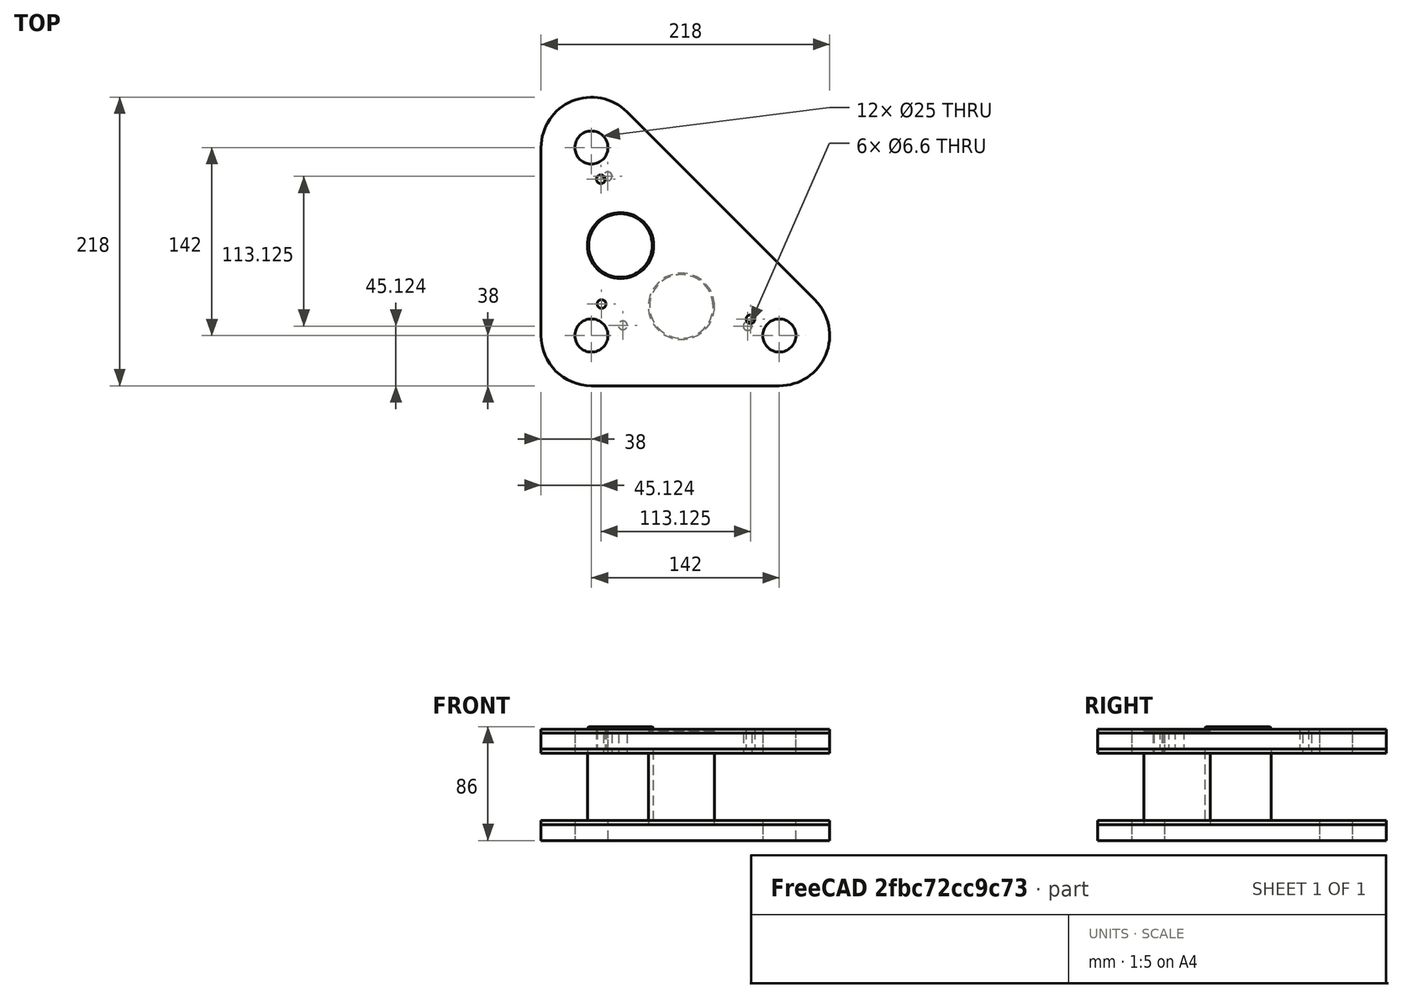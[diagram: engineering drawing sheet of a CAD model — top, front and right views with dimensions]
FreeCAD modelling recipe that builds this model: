
FCSTD DOCUMENT  (FreeCAD 0.21R33668 +26 (Git))
Label: hovairGuidageTriangle
License: All rights reserved
LicenseURL: http://en.wikipedia.org/wiki/All_rights_reserved
objects: TechDraw::DrawViewDimension×35, TechDraw::DrawViewAnnotation×11, Sketcher::SketchObject×9, PartDesign::Pad×6, TechDraw::DrawProjGroupItem×5, TechDraw::DrawSVGTemplate×3, TechDraw::DrawProjGroup×3, TechDraw::DrawViewSection×3, TechDraw::DrawPage×3, PartDesign::Plane×2, PartDesign::Hole×2, PartDesign::Chamfer×2, PartDesign::Body×2, TechDraw::DrawViewBalloon×1
note: 91 computed .brp shape members not serialized (recipe doc carries the construction recipe); baked Part::Feature solids carry a one-line shape summary decoded from their .brp

FEATURE [Sketcher::SketchObject] Sketch006
  FullyConstrained = true
  MapMode = 5
  Support = -> [XY_Plane003]
  sketch-geometry (10):
    g0: ArcOfCircle CenterX=38 CenterY=38 CenterZ=0 NormalX=0 NormalY=0 NormalZ=1 AngleXU=0 Radius=38 StartAngle=3.14159 EndAngle=4.71239
    g1: ArcOfCircle CenterX=180 CenterY=38 CenterZ=0 NormalX=0 NormalY=0 NormalZ=1 AngleXU=0 Radius=38 StartAngle=4.71239 EndAngle=7.06858
    g2: LineSegment StartX=38 StartY=0 StartZ=0 EndX=180 EndY=0 EndZ=0
    g3: ArcOfCircle CenterX=38 CenterY=180 CenterZ=0 NormalX=0 NormalY=0 NormalZ=1 AngleXU=0 Radius=38 StartAngle=0.785398 EndAngle=3.14159
    g4: LineSegment StartX=64.8701 StartY=206.87 StartZ=0 EndX=206.87 EndY=64.8701 EndZ=0
    g5: LineSegment StartX=0 StartY=180 StartZ=0 EndX=0 EndY=38 EndZ=0
    g6: Circle CenterX=38 CenterY=180 CenterZ=0 NormalX=0 NormalY=0 NormalZ=1 AngleXU=0 Radius=12.5
    g7: Circle CenterX=180 CenterY=38 CenterZ=0 NormalX=0 NormalY=0 NormalZ=1 AngleXU=0 Radius=12.5
    g8: Circle CenterX=38 CenterY=38 CenterZ=0 NormalX=0 NormalY=0 NormalZ=1 AngleXU=0 Radius=12.5
    g9: Circle CenterX=106 CenterY=60 CenterZ=0 NormalX=0 NormalY=0 NormalZ=1 AngleXU=0 Radius=25
  constraints (26):
    c: Radius(g0) = 38
    c: Tangent(g0,g-2) = 1.5708
    c: Tangent(g0,g-1) = -1.5708
    c: Radius(g1) = 38
    c: Tangent(g1,g-1) = -1.5708
    c: Distance(g0,g1) = 142
    c: Coincident(g2,g1)
    c: Coincident(g2,g0)
    c: Radius(g3) = 38
    c: Tangent(g3,g-2) = 1.5708
    c: Tangent(g1,g4) = 1.5708
    c: Tangent(g3,g4) = 1.5708
    c: Coincident(g5,g0)
    c: Coincident(g5,g3)
    c: Coincident(g4,g3)
    c: Coincident(g4,g1)
    c: Distance(g0,g3) = 142
    c: Coincident(g3,g6)
    c: Diameter(g6) = 25
    c: Coincident(g7,g1)
    c: Diameter(g7) = 25
    c: Coincident(g8,g0)
    c: Diameter(g8) = 25
    c: Diameter(g9) = 50
    c: DistanceY(g0,g9) = 60
    c: DistanceX(g0,g9) = 106
FEATURE [PartDesign::Pad] Pad001  label="base de fixation des axes"
  Direction = (0,0,1)
  Length = 12
  Length2 = 10
  Profile = -> Sketch006
  ReferenceAxis = -> Sketch006 [N_Axis]
  Type = 0
FEATURE [Sketcher::SketchObject] Sketch
  ExternalGeometry = -> [Sketch006]
  FullyConstrained = true
  MapMode = 5
  Placement = pos=(0,0,0) rot=(1,0,0;3.14159rad)
  Support = -> [Pad001]
  sketch-geometry (1):
    g0: Circle CenterX=106 CenterY=-60 CenterZ=0 NormalX=0 NormalY=0 NormalZ=1 AngleXU=0 Radius=25
  constraints (2):
    c: Coincident(g0,g-3)
    c: Equal(g0,g-3)
FEATURE [PartDesign::Pad] Pad  label="Entretoise"
  BaseFeature = -> Pad001
  Direction = (0,0,-1)
  Length = 83
  Length2 = 10
  Profile = -> Sketch
  ReferenceAxis = -> Sketch [N_Axis]
  Reversed = true
  Type = 0
FEATURE [PartDesign::Plane] DatumPlane  label="planBase"
  AttachmentOffset = pos=(0,0,54) rot=(0,0,1;0rad)
  Length = 60
  MapMode = 5
  Placement = pos=(0,0,66) rot=(0,0,1;0rad)
  ResizeMode = 0
  Support = -> [Pad]
  Width = 60
FEATURE [Sketcher::SketchObject] Sketch007
  FullyConstrained = true
  MapMode = 5
  Placement = pos=(0,0,66) rot=(0,0,1;0rad)
  Support = -> [DatumPlane]
  expr: Constraints[0] = Sketch006.Constraints[0]
  expr: Constraints[16] = Sketch006.Constraints[16]
  expr: Constraints[18] = Sketch006.Constraints[18]
  expr: Constraints[20] = Sketch006.Constraints[20]
  expr: Constraints[22] = Sketch006.Constraints[22]
  expr: Constraints[23] = Sketch006.Constraints[23]
  expr: Constraints[24] = Sketch006.Constraints[24]
  expr: Constraints[25] = Sketch006.Constraints[25]
  expr: Constraints[3] = Sketch006.Constraints[3]
  expr: Constraints[5] = Sketch006.Constraints[5]
  expr: Constraints[8] = Sketch006.Constraints[8]
  sketch-geometry (10):
    g0: ArcOfCircle CenterX=38 CenterY=38 CenterZ=0 NormalX=0 NormalY=0 NormalZ=1 AngleXU=0 Radius=38 StartAngle=3.14159 EndAngle=4.71239
    g1: ArcOfCircle CenterX=180 CenterY=38 CenterZ=0 NormalX=0 NormalY=0 NormalZ=1 AngleXU=0 Radius=38 StartAngle=4.71239 EndAngle=7.06858
    g2: LineSegment StartX=38 StartY=0 StartZ=0 EndX=180 EndY=0 EndZ=0
    g3: ArcOfCircle CenterX=38 CenterY=180 CenterZ=0 NormalX=0 NormalY=0 NormalZ=1 AngleXU=0 Radius=38 StartAngle=0.785398 EndAngle=3.14159
    g4: LineSegment StartX=64.8701 StartY=206.87 StartZ=0 EndX=206.87 EndY=64.8701 EndZ=0
    g5: LineSegment StartX=0 StartY=180 StartZ=0 EndX=0 EndY=38 EndZ=0
    g6: Circle CenterX=38 CenterY=180 CenterZ=0 NormalX=0 NormalY=0 NormalZ=1 AngleXU=0 Radius=12.5
    g7: Circle CenterX=180 CenterY=38 CenterZ=0 NormalX=0 NormalY=0 NormalZ=1 AngleXU=0 Radius=12.5
    g8: Circle CenterX=38 CenterY=38 CenterZ=0 NormalX=0 NormalY=0 NormalZ=1 AngleXU=0 Radius=12.5
    g9: Circle CenterX=106 CenterY=60 CenterZ=0 NormalX=0 NormalY=0 NormalZ=1 AngleXU=0 Radius=25
  constraints (26):
    c: Radius(g0) = 38
    c: Tangent(g0,g-2) = 1.5708
    c: Tangent(g0,g-1) = -1.5708
    c: Radius(g1) = 38
    c: Tangent(g1,g-1) = -1.5708
    c: Distance(g0,g1) = 142
    c: Coincident(g2,g1)
    c: Coincident(g2,g0)
    c: Radius(g3) = 38
    c: Tangent(g3,g-2) = 1.5708
    c: Tangent(g1,g4) = 1.5708
    c: Tangent(g3,g4) = 1.5708
    c: Coincident(g5,g0)
    c: Coincident(g5,g3)
    c: Coincident(g4,g3)
    c: Coincident(g4,g1)
    c: Distance(g0,g3) = 142
    c: Coincident(g3,g6)
    c: Diameter(g6) = 25
    c: Coincident(g7,g1)
    c: Diameter(g7) = 25
    c: Coincident(g8,g0)
    c: Diameter(g8) = 25
    c: Diameter(g9) = 50
    c: DistanceY(g0,g9) = 60
    c: DistanceX(g0,g9) = 106
FEATURE [PartDesign::Pad] Pad002
  BaseFeature = -> Pad
  Direction = (0,0,1)
  Length = 15
  Length2 = 10
  Profile = -> Sketch007
  ReferenceAxis = -> Sketch007 [N_Axis]
  Type = 0
FEATURE [Sketcher::SketchObject] Sketch008
  ExternalGeometry = -> [Pad002]
  FullyConstrained = false
  MapMode = 5
  Placement = pos=(0,0,81) rot=(0,0,1;0rad)
  Support = -> [Pad002]
  sketch-geometry (9):
    g0: LineSegment StartX=-92.9805 StartY=411.142 StartZ=0 EndX=245.063 EndY=-185.406 EndZ=0
    g1: LineSegment StartX=243.321 StartY=104.427 StartZ=0 EndX=-106.422 EndY=-8.72462 EndZ=0
    g2: LineSegment StartX=-89.2896 StartY=118.059 StartZ=0 EndX=316.645 EndY=-2.62407 EndZ=0
    g3: GeomPoint X=50.3253 Y=158.249 Z=0
    g4: GeomPoint X=61.7861 Y=45.6955 Z=0
    g5: GeomPoint X=156.037 Y=45.1243 Z=0
    g6: Circle CenterX=50.3253 CenterY=158.249 CenterZ=0 NormalX=0 NormalY=0 NormalZ=1 AngleXU=0 Radius=2.5
    g7: Circle CenterX=156.037 CenterY=45.1243 CenterZ=0 NormalX=0 NormalY=0 NormalZ=1 AngleXU=0 Radius=2.5
    g8: Circle CenterX=61.7861 CenterY=45.6955 CenterZ=0 NormalX=0 NormalY=0 NormalZ=1 AngleXU=0 Radius=2.5
  constraints (18):
    c: PointOnObject(g-3,g0)
    c: PointOnObject(g-6,g0)
    c: PointOnObject(g-6,g1)
    c: PointOnObject(g-4,g1)
    c: PointOnObject(g-5,g2)
    c: PointOnObject(g-6,g2)
    c: PointOnObject(g5,g2)
    c: PointOnObject(g3,g0)
    c: PointOnObject(g4,g1)
    c: Distance(g4,g-4) = 25
    c: Distance(g5,g-5) = 25
    c: Distance(g3,g-3) = 25
    c: Coincident(g6,g3)
    c: Coincident(g7,g5)
    c: Coincident(g8,g4)
    c: Diameter(g8) = 5
    c: Equal(g8,g6)
    c: Equal(g8,g7)
FEATURE [PartDesign::Hole] Hole
  BaseFeature = -> Pad002
  CustomThreadClearance = 0
  Depth = 15
  DepthType = 0
  Diameter = 6.6
  DrillForDepth = false
  DrillPoint = 1
  DrillPointAngle = 118
  HoleCutCountersinkAngle = 90
  HoleCutCustomValues = false
  HoleCutDepth = 0
  HoleCutDiameter = 0
  HoleCutType = 0
  ModelThread = false
  Profile = -> Sketch008
  Tapered = false
  TaperedAngle = 90
  ThreadClass = 0
  ThreadDepth = 15
  ThreadDepthType = 0
  ThreadDirection = 0
  ThreadFit = 0
  ThreadSize = 14
  ThreadType = 1
  Threaded = false
  UseCustomThreadClearance = false
FEATURE [PartDesign::Chamfer] Chamfer
  Angle = 45
  Base = -> Hole [Edge70]
  BaseFeature = -> Hole
  ChamferType = 0
  FlipDirection = false
  Size = 1
  Size2 = 1
  SupportTransform = false
  UseAllEdges = false
FEATURE [Sketcher::SketchObject] Sketch010
  FullyConstrained = true
  MapMode = 5
  Support = -> [XY_Plane004]
  sketch-geometry (10):
    g0: ArcOfCircle CenterX=38 CenterY=38 CenterZ=0 NormalX=0 NormalY=0 NormalZ=1 AngleXU=0 Radius=38 StartAngle=3.14159 EndAngle=4.71239
    g1: ArcOfCircle CenterX=180 CenterY=38 CenterZ=0 NormalX=0 NormalY=0 NormalZ=1 AngleXU=0 Radius=38 StartAngle=4.71239 EndAngle=7.06858
    g2: LineSegment StartX=38 StartY=0 StartZ=0 EndX=180 EndY=0 EndZ=0
    g3: ArcOfCircle CenterX=38 CenterY=180 CenterZ=0 NormalX=0 NormalY=0 NormalZ=1 AngleXU=0 Radius=38 StartAngle=0.785398 EndAngle=3.14159
    g4: LineSegment StartX=64.8701 StartY=206.87 StartZ=0 EndX=206.87 EndY=64.8701 EndZ=0
    g5: LineSegment StartX=0 StartY=180 StartZ=0 EndX=0 EndY=38 EndZ=0
    g6: Circle CenterX=38 CenterY=180 CenterZ=0 NormalX=0 NormalY=0 NormalZ=1 AngleXU=0 Radius=12.5
    g7: Circle CenterX=180 CenterY=38 CenterZ=0 NormalX=0 NormalY=0 NormalZ=1 AngleXU=0 Radius=12.5
    g8: Circle CenterX=38 CenterY=38 CenterZ=0 NormalX=0 NormalY=0 NormalZ=1 AngleXU=0 Radius=12.5
    g9: Circle CenterX=60 CenterY=106 CenterZ=0 NormalX=0 NormalY=0 NormalZ=1 AngleXU=0 Radius=25
  constraints (26):
    c: Radius(g0) = 38
    c: Tangent(g0,g-2) = 1.5708
    c: Tangent(g0,g-1) = -1.5708
    c: Radius(g1) = 38
    c: Tangent(g1,g-1) = -1.5708
    c: Distance(g0,g1) = 142
    c: Coincident(g2,g1)
    c: Coincident(g2,g0)
    c: Radius(g3) = 38
    c: Tangent(g3,g-2) = 1.5708
    c: Tangent(g1,g4) = 1.5708
    c: Tangent(g3,g4) = 1.5708
    c: Coincident(g5,g0)
    c: Coincident(g5,g3)
    c: Coincident(g4,g3)
    c: Coincident(g4,g1)
    c: Distance(g0,g3) = 142
    c: Coincident(g3,g6)
    c: Diameter(g6) = 25
    c: Coincident(g7,g1)
    c: Diameter(g7) = 25
    c: Coincident(g8,g0)
    c: Diameter(g8) = 25
    c: Diameter(g9) = 50
    c: DistanceY(g0,g9) = 106
    c: DistanceX(g0,g9) = 60
FEATURE [PartDesign::Pad] Pad004  label="base de fixation des axes001"
  Direction = (0,0,1)
  Length = 15
  Length2 = 10
  Profile = -> Sketch010
  ReferenceAxis = -> Sketch010 [N_Axis]
  Type = 0
FEATURE [Sketcher::SketchObject] Sketch009
  ExternalGeometry = -> [Sketch010]
  FullyConstrained = true
  MapMode = 5
  Placement = pos=(0,0,0) rot=(1,0,0;3.14159rad)
  Support = -> [Pad004]
  sketch-geometry (1):
    g0: Circle CenterX=60 CenterY=-106 CenterZ=0 NormalX=0 NormalY=0 NormalZ=1 AngleXU=0 Radius=25
  constraints (2):
    c: Coincident(g0,g-3)
    c: Equal(g0,g-3)
FEATURE [PartDesign::Pad] Pad003  label="Entretoise001"
  BaseFeature = -> Pad004
  Direction = (0,0,-1)
  Length = 86
  Length2 = 10
  Profile = -> Sketch009
  ReferenceAxis = -> Sketch009 [N_Axis]
  Reversed = true
  Type = 0
FEATURE [PartDesign::Plane] DatumPlane001  label="planBase001"
  AttachmentOffset = pos=(0,0,54) rot=(0,0,1;0rad)
  Length = 60
  MapMode = 5
  Placement = pos=(0,0,69) rot=(0,0,1;0rad)
  ResizeMode = 0
  Support = -> [Pad003]
  Width = 60
FEATURE [Sketcher::SketchObject] Sketch011
  FullyConstrained = true
  MapMode = 5
  Placement = pos=(0,0,69) rot=(0,0,1;0rad)
  Support = -> [DatumPlane001]
  expr: Constraints[0] = Sketch010.Constraints[0]
  expr: Constraints[16] = Sketch010.Constraints[16]
  expr: Constraints[18] = Sketch010.Constraints[18]
  expr: Constraints[20] = Sketch010.Constraints[20]
  expr: Constraints[22] = Sketch010.Constraints[22]
  expr: Constraints[23] = Sketch010.Constraints[23]
  expr: Constraints[24] = Sketch010.Constraints[24]
  expr: Constraints[25] = Sketch010.Constraints[25]
  expr: Constraints[3] = Sketch010.Constraints[3]
  expr: Constraints[5] = Sketch010.Constraints[5]
  expr: Constraints[8] = Sketch010.Constraints[8]
  sketch-geometry (10):
    g0: ArcOfCircle CenterX=38 CenterY=38 CenterZ=0 NormalX=0 NormalY=0 NormalZ=1 AngleXU=0 Radius=38 StartAngle=3.14159 EndAngle=4.71239
    g1: ArcOfCircle CenterX=180 CenterY=38 CenterZ=0 NormalX=0 NormalY=0 NormalZ=1 AngleXU=0 Radius=38 StartAngle=4.71239 EndAngle=7.06858
    g2: LineSegment StartX=38 StartY=0 StartZ=0 EndX=180 EndY=0 EndZ=0
    g3: ArcOfCircle CenterX=38 CenterY=180 CenterZ=0 NormalX=0 NormalY=0 NormalZ=1 AngleXU=0 Radius=38 StartAngle=0.785398 EndAngle=3.14159
    g4: LineSegment StartX=64.8701 StartY=206.87 StartZ=0 EndX=206.87 EndY=64.8701 EndZ=0
    g5: LineSegment StartX=0 StartY=180 StartZ=0 EndX=0 EndY=38 EndZ=0
    g6: Circle CenterX=38 CenterY=180 CenterZ=0 NormalX=0 NormalY=0 NormalZ=1 AngleXU=0 Radius=12.5
    g7: Circle CenterX=180 CenterY=38 CenterZ=0 NormalX=0 NormalY=0 NormalZ=1 AngleXU=0 Radius=12.5
    g8: Circle CenterX=38 CenterY=38 CenterZ=0 NormalX=0 NormalY=0 NormalZ=1 AngleXU=0 Radius=12.5
    g9: Circle CenterX=60 CenterY=106 CenterZ=0 NormalX=0 NormalY=0 NormalZ=1 AngleXU=0 Radius=25
  constraints (26):
    c: Radius(g0) = 38
    c: Tangent(g0,g-2) = 1.5708
    c: Tangent(g0,g-1) = -1.5708
    c: Radius(g1) = 38
    c: Tangent(g1,g-1) = -1.5708
    c: Distance(g0,g1) = 142
    c: Coincident(g2,g1)
    c: Coincident(g2,g0)
    c: Radius(g3) = 38
    c: Tangent(g3,g-2) = 1.5708
    c: Tangent(g1,g4) = 1.5708
    c: Tangent(g3,g4) = 1.5708
    c: Coincident(g5,g0)
    c: Coincident(g5,g3)
    c: Coincident(g4,g3)
    c: Coincident(g4,g1)
    c: Distance(g0,g3) = 142
    c: Coincident(g3,g6)
    c: Diameter(g6) = 25
    c: Coincident(g7,g1)
    c: Diameter(g7) = 25
    c: Coincident(g8,g0)
    c: Diameter(g8) = 25
    c: Diameter(g9) = 50
    c: DistanceY(g0,g9) = 106
    c: DistanceX(g0,g9) = 60
FEATURE [PartDesign::Pad] Pad005
  BaseFeature = -> Pad003
  Direction = (0,0,1)
  Length = 15
  Length2 = 10
  Profile = -> Sketch011
  ReferenceAxis = -> Sketch011 [N_Axis]
  Type = 0
FEATURE [Sketcher::SketchObject] Sketch012
  ExternalGeometry = -> [Pad005]
  FullyConstrained = false
  MapMode = 5
  Placement = pos=(0,0,84) rot=(0,0,1;0rad)
  Support = -> [Pad005]
  sketch-geometry (9):
    g0: LineSegment StartX=-29.8325 StartY=408.164 StartZ=0 EndX=147.908 EndY=-189.691 EndZ=0
    g1: LineSegment StartX=139.234 StartY=350.905 StartZ=0 EndX=-31.2765 EndY=-176.127 EndZ=0
    g2: LineSegment StartX=-79.9504 StartY=185.305 StartZ=0 EndX=317.641 EndY=-39.9967 EndZ=0
    g3: GeomPoint X=45.1243 Y=156.037 Z=0
    g4: GeomPoint X=45.6955 Y=61.7861 Z=0
    g5: GeomPoint X=158.249 Y=50.3253 Z=0
    g6: Circle CenterX=45.1243 CenterY=156.037 CenterZ=0 NormalX=0 NormalY=0 NormalZ=1 AngleXU=0 Radius=2.5
    g7: Circle CenterX=158.249 CenterY=50.3253 CenterZ=0 NormalX=0 NormalY=0 NormalZ=1 AngleXU=0 Radius=2.5
    g8: Circle CenterX=45.6955 CenterY=61.7861 CenterZ=0 NormalX=0 NormalY=0 NormalZ=1 AngleXU=0 Radius=2.5
  constraints (18):
    c: PointOnObject(g-3,g0)
    c: PointOnObject(g-6,g0)
    c: PointOnObject(g-6,g1)
    c: PointOnObject(g-4,g1)
    c: PointOnObject(g-5,g2)
    c: PointOnObject(g-6,g2)
    c: PointOnObject(g5,g2)
    c: PointOnObject(g3,g0)
    c: PointOnObject(g4,g1)
    c: Distance(g4,g-4) = 25
    c: Distance(g5,g-5) = 25
    c: Distance(g3,g-3) = 25
    c: Coincident(g6,g3)
    c: Coincident(g7,g5)
    c: Coincident(g8,g4)
    c: Diameter(g8) = 5
    c: Equal(g8,g6)
    c: Equal(g8,g7)
FEATURE [PartDesign::Hole] Hole001
  BaseFeature = -> Pad005
  CustomThreadClearance = 0
  Depth = 15
  DepthType = 0
  Diameter = 6.6
  DrillForDepth = false
  DrillPoint = 1
  DrillPointAngle = 118
  HoleCutCountersinkAngle = 90
  HoleCutCustomValues = false
  HoleCutDepth = 0
  HoleCutDiameter = 6.1
  HoleCutType = 0
  ModelThread = false
  Profile = -> Sketch012
  Tapered = false
  TaperedAngle = 90
  ThreadClass = 0
  ThreadDepth = 15
  ThreadDepthType = 0
  ThreadDirection = 0
  ThreadFit = 0
  ThreadSize = 14
  ThreadType = 1
  Threaded = false
  UseCustomThreadClearance = false
FEATURE [PartDesign::Chamfer] Chamfer001
  Angle = 45
  Base = -> Hole001 [Edge70]
  BaseFeature = -> Hole001
  ChamferType = 0
  FlipDirection = false
  Size = 1
  Size2 = 1
  SupportTransform = false
  UseAllEdges = false
FEATURE [PartDesign::Body] Body003  label="triangleGauche"
  Group = -> [Sketch010,Pad004,Sketch009,Pad003,DatumPlane001,Sketch011,Pad005,Sketch012,Hole001,Chamfer001]
  Origin = -> Origin004
  Tip = -> Chamfer001
FEATURE [TechDraw::DrawSVGTemplate] Template
  EditableTexts = Designed_by_Name=Designed by Name; Drawing_number=Drawing number; FC-Date=Date; FC-SC=Scale; FC-SH=Sheet; FC-Title=Title; Subtitle=Subtitle; Weight=Weight
  Height = 210
  Orientation = 1
  Width = 297
  expr: Label = Template
FEATURE [TechDraw::DrawProjGroupItem] ProjItem  label="Front"
  CoarseView = false
  Direction = (0,0,1)
  Focus = 100
  HardHidden = false
  IsoCount = 0
  IsoHidden = false
  IsoVisible = true
  LockPosition = true
  Perspective = false
  Rotation = 0
  RotationVector = (-1,0,0)
  Scale = 0.5
  ScaleType = 2
  ScrubCount = 0
  SeamHidden = false
  SeamVisible = true
  SmoothHidden = false
  SmoothVisible = true
  Source = -> [Chamfer]
  Type = 0
  X = 0
  XDirection = (2e-16,-1,0)
  Y = 0
FEATURE [TechDraw::DrawProjGroupItem] ProjItem001  label="Left"
  CoarseView = false
  Direction = (-2e-16,1,1e-16)
  Focus = 100
  HardHidden = false
  IsoCount = 0
  IsoHidden = false
  IsoVisible = true
  LockPosition = false
  Perspective = false
  Rotation = 0
  RotationVector = (1,0,0)
  ScaleType = 2
  ScrubCount = 0
  SeamHidden = false
  SeamVisible = true
  SmoothHidden = false
  SmoothVisible = true
  Source = -> [Chamfer]
  Type = 1
  X = 90.25
  XDirection = (0,-1e-16,1)
  Y = 0
FEATURE [TechDraw::DrawProjGroup] ProjGroup
  Anchor = -> ProjItem
  AutoDistribute = true
  LockPosition = false
  ProjectionType = 0
  Rotation = 0
  Scale = 0.5
  ScaleType = 0
  Source = -> [Chamfer]
  Views = -> [ProjItem,ProjItem001]
  X = 94.985
  Y = 133.767
  spacingX = 15
  spacingY = 15
FEATURE [TechDraw::DrawViewDimension] Dimension
  AngleOverride = false
  Arbitrary = false
  ArbitraryTolerances = false
  EqualTolerance = true
  ExtensionAngle = 0
  FormatSpec = %.2w
  FormatSpecOverTolerance = %+.2w
  FormatSpecUnderTolerance = %+.2w
  Inverted = false
  LineAngle = 0
  LockPosition = false
  MeasureType = 1
  OverTolerance = 0
  References2D = -> [ProjItem001]
  Rotation = 0
  Scale = 0.5
  ScaleType = 0
  TheoreticalExact = false
  Type = 1
  UnderTolerance = 0
  X = -2.20172
  Y = -62.1546
FEATURE [TechDraw::DrawViewDimension] Dimension003
  AngleOverride = false
  Arbitrary = false
  ArbitraryTolerances = false
  EqualTolerance = true
  ExtensionAngle = 0
  FormatSpec = %.2w
  FormatSpecOverTolerance = %+.2w
  FormatSpecUnderTolerance = %+.2w
  Inverted = false
  LineAngle = 0
  LockPosition = false
  MeasureType = 1
  OverTolerance = 0
  References2D = -> [ProjItem001]
  Rotation = 0
  Scale = 0.5
  ScaleType = 0
  TheoreticalExact = false
  Type = 1
  UnderTolerance = 0
  X = 51.2517
  Y = 24.673
FEATURE [Sketcher::SketchObject] Sketch013
  ExternalGeometry = -> [Chamfer]
  FullyConstrained = false
  MapMode = 5
  Placement = pos=(0,0,81) rot=(0,0,1;0rad)
  Support = -> [Chamfer]
  sketch-geometry (5):
    g0: LineSegment StartX=0 StartY=158.249 StartZ=0 EndX=50.3253 EndY=158.249 EndZ=0
    g1: LineSegment StartX=50.3253 StartY=158.249 StartZ=0 EndX=50.3253 EndY=45.6955 EndZ=0
    g2: LineSegment StartX=50.3253 StartY=45.6955 StartZ=0 EndX=144.123 EndY=45.6955 EndZ=0
    g3: LineSegment StartX=144.123 StartY=45.1243 StartZ=0 EndX=236.221 EndY=45.1243 EndZ=0
    g4: LineSegment StartX=144.123 StartY=45.6955 StartZ=0 EndX=144.123 EndY=45.1243 EndZ=0
  constraints (13):
    c: Coincident(g0,g-3)
    c: Horizontal(g0)
    c: PointOnObject(g0,g-2)
    c: Coincident(g1,g0)
    c: Vertical(g1)
    c: Coincident(g2,g1)
    c: PointOnObject(g-4,g2)
    c: Horizontal(g2)
    c: Horizontal(g3)
    c: PointOnObject(g-5,g3)
    c: Coincident(g4,g3)
    c: Coincident(g2,g4)
    c: Vertical(g4)
FEATURE [PartDesign::Body] Body002  label="triangle droit"
  Group = -> [Sketch006,Pad001,Sketch,Pad,DatumPlane,Sketch007,Pad002,Sketch008,Hole,Chamfer,Sketch013]
  Origin = -> Origin003
  Tip = -> Chamfer
FEATURE [TechDraw::DrawViewDimension] Dimension004
  AngleOverride = false
  Arbitrary = false
  ArbitraryTolerances = false
  EqualTolerance = true
  ExtensionAngle = 0
  FormatSpec = R%.2w
  FormatSpecOverTolerance = %+.2w
  FormatSpecUnderTolerance = %+.2w
  Inverted = false
  LineAngle = 0
  LockPosition = false
  MeasureType = 1
  OverTolerance = 0
  References2D = -> [ProjItem]
  Rotation = 0
  Scale = 0.5
  ScaleType = 0
  TheoreticalExact = false
  Type = 4
  UnderTolerance = 0
  X = 54.0861
  Y = 56.9792
FEATURE [TechDraw::DrawViewDimension] Dimension005
  AngleOverride = false
  Arbitrary = true
  ArbitraryTolerances = false
  EqualTolerance = true
  ExtensionAngle = 0
  FormatSpec = M6
  FormatSpecOverTolerance = %+.2w
  FormatSpecUnderTolerance = %+.2w
  Inverted = false
  LineAngle = 0
  LockPosition = false
  MeasureType = 1
  OverTolerance = 0
  References2D = -> [ProjItem]
  Rotation = 0
  Scale = 0.5
  ScaleType = 0
  TheoreticalExact = false
  Type = 5
  UnderTolerance = 0
  X = 13.1733
  Y = 30.3827
FEATURE [TechDraw::DrawViewDimension] Dimension006
  AngleOverride = false
  Arbitrary = false
  ArbitraryTolerances = false
  EqualTolerance = true
  ExtensionAngle = 0
  FormatSpec = ⌀%.2w
  FormatSpecOverTolerance = %+.2w
  FormatSpecUnderTolerance = %+.2w
  Inverted = false
  LineAngle = 0
  LockPosition = false
  MeasureType = 1
  OverTolerance = 0
  References2D = -> [ProjItem]
  Rotation = 0
  Scale = 0.5
  ScaleType = 0
  TheoreticalExact = false
  Type = 5
  UnderTolerance = 0
  X = 18.3828
  Y = 42.1273
FEATURE [TechDraw::DrawViewDimension] Dimension007
  AngleOverride = false
  Arbitrary = true
  ArbitraryTolerances = false
  EqualTolerance = true
  ExtensionAngle = 0
  FormatSpec = 200
  Inverted = false
  LineAngle = 0
  LockPosition = false
  MeasureType = 1
  OverTolerance = 0
  References2D = -> [ProjItem]
  Rotation = 0
  Scale = 0.5
  ScaleType = 0
  TheoreticalExact = false
  Type = 0
  UnderTolerance = 0
  X = -18.8935
  Y = 32.6274
FEATURE [TechDraw::DrawViewDimension] Dimension008
  AngleOverride = false
  Arbitrary = false
  ArbitraryTolerances = false
  EqualTolerance = true
  ExtensionAngle = 0
  FormatSpec = %.2w
  FormatSpecOverTolerance = %+.2w
  FormatSpecUnderTolerance = %+.2w
  Inverted = false
  LineAngle = 0
  LockPosition = false
  MeasureType = 1
  OverTolerance = 0
  References2D = -> [ProjItem]
  Rotation = 0
  Scale = 0.5
  ScaleType = 0
  TheoreticalExact = false
  Type = 2
  UnderTolerance = 0
  X = 66.2444
  Y = -39.7903
FEATURE [TechDraw::DrawViewDimension] Dimension009
  AngleOverride = false
  Arbitrary = false
  ArbitraryTolerances = false
  EqualTolerance = true
  ExtensionAngle = 0
  FormatSpec = %.2w
  FormatSpecOverTolerance = %+.2w
  FormatSpecUnderTolerance = %+.2w
  Inverted = false
  LineAngle = 0
  LockPosition = false
  MeasureType = 1
  OverTolerance = 0
  References2D = -> [ProjItem]
  Rotation = 0
  Scale = 0.5
  ScaleType = 0
  TheoreticalExact = false
  Type = 2
  UnderTolerance = 0
  X = 66.4544
  Y = -1.17084
FEATURE [TechDraw::DrawViewDimension] Dimension010
  AngleOverride = false
  Arbitrary = false
  ArbitraryTolerances = false
  EqualTolerance = true
  ExtensionAngle = 0
  FormatSpec = %.2w
  FormatSpecOverTolerance = %+.2w
  FormatSpecUnderTolerance = %+.2w
  Inverted = false
  LineAngle = 0
  LockPosition = false
  MeasureType = 1
  OverTolerance = 0
  References2D = -> [ProjItem]
  Rotation = 0
  Scale = 0.5
  ScaleType = 0
  TheoreticalExact = false
  Type = 1
  UnderTolerance = 0
  X = 45.6795
  Y = -66.2972
FEATURE [TechDraw::DrawViewDimension] Dimension011
  AngleOverride = false
  Arbitrary = false
  ArbitraryTolerances = false
  EqualTolerance = true
  ExtensionAngle = 0
  FormatSpec = %.2w
  FormatSpecOverTolerance = %+.2w
  FormatSpecUnderTolerance = %+.2w
  Inverted = false
  LineAngle = 0
  LockPosition = false
  MeasureType = 1
  OverTolerance = 0
  References2D = -> [ProjItem]
  Rotation = 0
  Scale = 0.5
  ScaleType = 0
  TheoreticalExact = false
  Type = 1
  UnderTolerance = 0
  X = 4.75673
  Y = -64.2585
FEATURE [TechDraw::DrawViewDimension] Dimension012
  AngleOverride = false
  Arbitrary = false
  ArbitraryTolerances = false
  EqualTolerance = true
  ExtensionAngle = 0
  FormatSpec = %.2w
  FormatSpecOverTolerance = %+.2w
  FormatSpecUnderTolerance = %+.2w
  Inverted = false
  LineAngle = 0
  LockPosition = false
  MeasureType = 1
  OverTolerance = 0
  References2D = -> [ProjItem]
  Rotation = 0
  Scale = 0.5
  ScaleType = 0
  TheoreticalExact = false
  Type = 1
  UnderTolerance = 0
  X = 39.9798
  Y = 21.4191
FEATURE [TechDraw::DrawViewDimension] Dimension013
  AngleOverride = false
  Arbitrary = false
  ArbitraryTolerances = false
  EqualTolerance = true
  ExtensionAngle = 0
  FormatSpec = ⌀%.2w
  FormatSpecOverTolerance = %+.2w
  FormatSpecUnderTolerance = %+.2w
  Inverted = false
  LineAngle = 0
  LockPosition = false
  MeasureType = 1
  OverTolerance = 0
  References2D = -> [ProjItem]
  Rotation = 0
  Scale = 0.5
  ScaleType = 0
  TheoreticalExact = false
  Type = 5
  UnderTolerance = 0
  X = -8.25965
  Y = 5.44612
FEATURE [TechDraw::DrawViewDimension] Dimension014
  AngleOverride = false
  Arbitrary = false
  ArbitraryTolerances = false
  EqualTolerance = true
  ExtensionAngle = 0
  FormatSpec = %.2w
  FormatSpecOverTolerance = %+.2w
  FormatSpecUnderTolerance = %+.2w
  Inverted = false
  LineAngle = 0
  LockPosition = false
  MeasureType = 1
  OverTolerance = 0
  References2D = -> [ProjItem]
  Rotation = 0
  Scale = 0.5
  ScaleType = 0
  TheoreticalExact = false
  Type = 2
  UnderTolerance = 0
  X = -4.86799
  Y = -24.4104
FEATURE [TechDraw::DrawViewDimension] Dimension015
  AngleOverride = false
  Arbitrary = false
  ArbitraryTolerances = false
  EqualTolerance = true
  ExtensionAngle = 0
  FormatSpec = %.2w
  FormatSpecOverTolerance = %+.2w
  FormatSpecUnderTolerance = %+.2w
  Inverted = false
  LineAngle = 0
  LockPosition = false
  MeasureType = 1
  OverTolerance = 0
  References2D = -> [ProjItem001]
  Rotation = 0
  Scale = 0.5
  ScaleType = 0
  TheoreticalExact = false
  Type = 1
  UnderTolerance = 0
  X = -1.58253
  Y = -51.3349
FEATURE [TechDraw::DrawViewDimension] Dimension016
  AngleOverride = false
  Arbitrary = false
  ArbitraryTolerances = false
  EqualTolerance = true
  ExtensionAngle = 0
  FormatSpec = %.2w
  FormatSpecOverTolerance = %+.2w
  FormatSpecUnderTolerance = %+.2w
  Inverted = false
  LineAngle = 0
  LockPosition = false
  MeasureType = 1
  OverTolerance = 0
  References2D = -> [ProjItem001]
  Rotation = 0
  Scale = 0.5
  ScaleType = 0
  TheoreticalExact = false
  Type = 1
  UnderTolerance = 0
  X = 28.9686
  Y = 65.6457
FEATURE [TechDraw::DrawViewDimension] Dimension017
  AngleOverride = false
  Arbitrary = false
  ArbitraryTolerances = false
  EqualTolerance = true
  ExtensionAngle = 0
  FormatSpec = %.2w
  FormatSpecOverTolerance = %+.2w
  FormatSpecUnderTolerance = %+.2w
  Inverted = false
  LineAngle = 0
  LockPosition = false
  MeasureType = 1
  OverTolerance = 0
  References2D = -> [ProjItem001]
  Rotation = 0
  Scale = 0.5
  ScaleType = 0
  TheoreticalExact = false
  Type = 1
  UnderTolerance = 0
  X = -31.0511
  Y = 64.9807
FEATURE [TechDraw::DrawViewDimension] Dimension018
  AngleOverride = false
  Arbitrary = false
  ArbitraryTolerances = false
  EqualTolerance = true
  ExtensionAngle = 0
  FormatSpec = %.2w x45°
  FormatSpecOverTolerance = %+.2w
  FormatSpecUnderTolerance = %+.2w
  Inverted = false
  LineAngle = 0
  LockPosition = false
  MeasureType = 1
  OverTolerance = 0
  References2D = -> [ProjItem001]
  Rotation = 0
  Scale = 0.5
  ScaleType = 0
  TheoreticalExact = false
  Type = 2
  UnderTolerance = 0
  X = 30.7283
  Y = -23.2941
FEATURE [TechDraw::DrawViewSection] SectionView  label="Section  - "
  BaseView = -> ProjItem
  CoarseView = false
  CutSurfaceDisplay = 2
  Direction = (1,1e-16,0)
  FileGeomPattern = C:/Program Files/FreeCAD 0.21/data/Mod/TechDraw/PAT/FCPAT.pat
  FileHatchPattern = C:/Program Files/FreeCAD 0.21/data/Mod/TechDraw/Patterns/simple.svg
  Focus = 100
  FuseBeforeCut = false
  HardHidden = false
  HatchOffset = (0,0,0)
  HatchRotation = 0
  HatchScale = 1
  IsoCount = 0
  IsoHidden = false
  IsoVisible = true
  LockPosition = false
  NameGeomPattern = Diamant
  Perspective = false
  Rotation = 0
  Scale = 0.5
  ScaleType = 2
  ScrubCount = 0
  SeamHidden = false
  SeamVisible = true
  SectionDirection = 4
  SectionNormal = (1,1e-16,0)
  SectionOrigin = (38,108,41.5)
  SmoothHidden = false
  SmoothVisible = true
  Source = -> [Chamfer]
  TrimAfterCut = false
  X = 79.928
  XDirection = (1e-16,-1,0)
  Y = 37.3303
FEATURE [TechDraw::DrawPage] Page
  KeepUpdated = true
  NextBalloonIndex = 1
  ProjectionType = 0
  Scale = 0.5
  Template = -> Template
  Views = -> [ProjGroup,Dimension,Dimension003,Dimension004,Dimension005,Dimension006,Dimension007,Dimension008,Dimension009,Dimension010,Dimension011,Dimension012,Dimension013,Dimension014,Dimension015,Dimension016,Dimension017,Dimension018,SectionView]
FEATURE [TechDraw::DrawSVGTemplate] Template001
  EditableTexts = A3=A3; A__=_________; B__=_________; C__=_________; D__=_________; E__=_________; Echelle=0,5; F__=_________; G__=_________; H__=_________; I__=_________; Societe=CAF; Sous_titre=DROIT; Titre=TRIANGLE HOVAIR
  Height = 297
  Orientation = 1
  Template = C:/Program Files/FreeCAD 0.21/data/Mod/TechDraw/Templates/A3_Landscape_FR_m52.svg
  Width = 420
FEATURE [TechDraw::DrawProjGroupItem] ProjItem002  label="Front001"
  CoarseView = false
  Direction = (0,0,1)
  Focus = 100
  HardHidden = false
  IsoCount = 0
  IsoHidden = false
  IsoVisible = true
  LockPosition = true
  Perspective = false
  Rotation = 0
  RotationVector = (1,0,0)
  Scale = 0.5
  ScaleType = 2
  ScrubCount = 0
  SeamHidden = false
  SeamVisible = true
  SmoothHidden = false
  SmoothVisible = true
  Source = -> [Body002]
  Type = 0
  X = 0
  XDirection = (1e-16,-1,0)
  Y = 0
FEATURE [TechDraw::DrawProjGroupItem] ProjItem003  label="Left001"
  CoarseView = false
  Direction = (-1e-16,1,1e-16)
  Focus = 100
  HardHidden = false
  IsoCount = 0
  IsoHidden = false
  IsoVisible = true
  LockPosition = true
  Perspective = false
  Rotation = 0
  RotationVector = (1,0,0)
  Scale = 0.5
  ScaleType = 2
  ScrubCount = 0
  SeamHidden = false
  SeamVisible = true
  SmoothHidden = false
  SmoothVisible = false
  Source = -> [Body002]
  Type = 1
  X = 159.01
  XDirection = (0,-1e-16,1)
  Y = 0
FEATURE [TechDraw::DrawProjGroup] ProjGroup001
  Anchor = -> ProjItem002
  AutoDistribute = true
  LockPosition = true
  ProjectionType = 0
  Rotation = 0
  Scale = 0.5
  ScaleType = 0
  Source = -> [Body002]
  Views = -> [ProjItem002,ProjItem003]
  X = 145.162
  Y = 186.721
  spacingX = 15
  spacingY = 15
FEATURE [TechDraw::DrawViewDimension] Dimension019
  AngleOverride = false
  Arbitrary = false
  ArbitraryTolerances = false
  EqualTolerance = true
  ExtensionAngle = 0
  FormatSpec = R%.2w
  FormatSpecOverTolerance = %+.2w
  FormatSpecUnderTolerance = %+.2w
  Inverted = false
  LineAngle = 0
  LockPosition = false
  MeasureType = 1
  OverTolerance = 0
  References2D = -> [ProjItem002]
  Rotation = 0
  Scale = 0.5
  ScaleType = 0
  TheoreticalExact = false
  Type = 4
  UnderTolerance = 0
  X = 54.9066
  Y = 61.5716
FEATURE [TechDraw::DrawViewDimension] Dimension020
  AngleOverride = false
  Arbitrary = false
  ArbitraryTolerances = false
  EqualTolerance = true
  ExtensionAngle = 0
  FormatSpec = %.2w
  FormatSpecOverTolerance = %+.2w
  FormatSpecUnderTolerance = %+.2w
  Inverted = false
  LineAngle = 0
  LockPosition = false
  MeasureType = 1
  OverTolerance = 0
  References2D = -> [ProjItem002]
  Rotation = 0
  Scale = 0.5
  ScaleType = 0
  TheoreticalExact = false
  Type = 2
  UnderTolerance = 0
  X = 71.9765
  Y = -41.5848
FEATURE [TechDraw::DrawViewDimension] Dimension021
  AngleOverride = false
  Arbitrary = false
  ArbitraryTolerances = false
  EqualTolerance = true
  ExtensionAngle = 0
  FormatSpec = %.2w
  FormatSpecOverTolerance = %+.2w
  FormatSpecUnderTolerance = %+.2w
  Inverted = false
  LineAngle = 0
  LockPosition = false
  MeasureType = 1
  OverTolerance = 0
  References2D = -> [ProjItem002]
  Rotation = 0
  Scale = 0.5
  ScaleType = 0
  TheoreticalExact = false
  Type = 2
  UnderTolerance = 0
  X = 72.0538
  Y = 2.10538
FEATURE [TechDraw::DrawViewDimension] Dimension022
  AngleOverride = false
  Arbitrary = false
  ArbitraryTolerances = false
  EqualTolerance = true
  ExtensionAngle = 0
  FormatSpec = ⌀%.2w
  FormatSpecOverTolerance = %+.2w
  FormatSpecUnderTolerance = %+.2w
  Inverted = false
  LineAngle = 0
  LockPosition = false
  MeasureType = 1
  OverTolerance = 0
  References2D = -> [ProjItem002]
  Rotation = 0
  Scale = 0.5
  ScaleType = 0
  TheoreticalExact = false
  Type = 5
  UnderTolerance = 0
  X = 18.893
  Y = 41.1341
FEATURE [TechDraw::DrawViewDimension] Dimension023
  AngleOverride = false
  Arbitrary = true
  ArbitraryTolerances = false
  EqualTolerance = true
  ExtensionAngle = 0
  FormatSpec = M6
  FormatSpecOverTolerance = %+.2w
  FormatSpecUnderTolerance = %+.2w
  Inverted = false
  LineAngle = 0
  LockPosition = false
  MeasureType = 1
  OverTolerance = 0
  References2D = -> [ProjItem002]
  Rotation = 0
  Scale = 0.5
  ScaleType = 0
  TheoreticalExact = false
  Type = 5
  UnderTolerance = 0
  X = 11.001
  Y = 29.1765
FEATURE [TechDraw::DrawViewDimension] Dimension024
  AngleOverride = false
  Arbitrary = false
  ArbitraryTolerances = false
  EqualTolerance = true
  ExtensionAngle = 0
  FormatSpec = %.2w
  FormatSpecOverTolerance = %+.2w
  FormatSpecUnderTolerance = %+.2w
  Inverted = false
  LineAngle = 0
  LockPosition = false
  MeasureType = 1
  OverTolerance = 0
  References2D = -> [ProjItem002]
  Rotation = 0
  Scale = 0.5
  ScaleType = 0
  TheoreticalExact = false
  Type = 1
  UnderTolerance = 0
  X = 45.6162
  Y = -63.3965
FEATURE [TechDraw::DrawViewDimension] Dimension025
  AngleOverride = false
  Arbitrary = false
  ArbitraryTolerances = false
  EqualTolerance = true
  ExtensionAngle = 0
  FormatSpec = %.2w
  FormatSpecOverTolerance = %+.2w
  FormatSpecUnderTolerance = %+.2w
  Inverted = false
  LineAngle = 0
  LockPosition = false
  MeasureType = 1
  OverTolerance = 0
  References2D = -> [ProjItem002]
  Rotation = 0
  Scale = 0.5
  ScaleType = 0
  TheoreticalExact = false
  Type = 1
  UnderTolerance = 0
  X = 5.08227
  Y = -63.2407
FEATURE [TechDraw::DrawViewDimension] Dimension026
  AngleOverride = false
  Arbitrary = false
  ArbitraryTolerances = false
  EqualTolerance = true
  ExtensionAngle = 0
  FormatSpec = %.2w
  FormatSpecOverTolerance = %+.2w
  FormatSpecUnderTolerance = %+.2w
  Inverted = false
  LineAngle = 0
  LockPosition = false
  MeasureType = 1
  OverTolerance = 0
  References2D = -> [ProjItem002]
  Rotation = 0
  Scale = 0.5
  ScaleType = 0
  TheoreticalExact = false
  Type = 1
  UnderTolerance = 0
  X = 39.166
  Y = 19.237
FEATURE [TechDraw::DrawViewDimension] Dimension027
  AngleOverride = false
  Arbitrary = false
  ArbitraryTolerances = false
  EqualTolerance = true
  ExtensionAngle = 0
  FormatSpec = ⌀%.2w
  FormatSpecOverTolerance = %+.2w
  FormatSpecUnderTolerance = %+.2w
  Inverted = false
  LineAngle = 0
  LockPosition = false
  MeasureType = 1
  OverTolerance = 0
  References2D = -> [ProjItem002]
  Rotation = 0
  Scale = 0.5
  ScaleType = 0
  TheoreticalExact = false
  Type = 5
  UnderTolerance = 0
  X = -8.21447
  Y = 4.0267
FEATURE [TechDraw::DrawViewDimension] Dimension028
  AngleOverride = false
  Arbitrary = false
  ArbitraryTolerances = false
  EqualTolerance = true
  ExtensionAngle = 0
  FormatSpec = %.2w
  FormatSpecOverTolerance = %+.2w
  FormatSpecUnderTolerance = %+.2w
  Inverted = false
  LineAngle = 0
  LockPosition = false
  MeasureType = 1
  OverTolerance = 0
  References2D = -> [ProjItem002]
  Rotation = 0
  Scale = 0.5
  ScaleType = 0
  TheoreticalExact = false
  Type = 2
  UnderTolerance = 0
  X = -0.479657
  Y = -24.8425
FEATURE [TechDraw::DrawViewSection] SectionView001  label="A - A"
  BaseView = -> ProjItem002
  CoarseView = false
  CutSurfaceDisplay = 2
  Direction = (1,0,0)
  FileGeomPattern = C:/Program Files/FreeCAD 0.21/data/Mod/TechDraw/PAT/FCPAT.pat
  FileHatchPattern = C:/Program Files/FreeCAD 0.21/data/Mod/TechDraw/Patterns/simple.svg
  Focus = 100
  FuseBeforeCut = false
  HardHidden = false
  HatchOffset = (0,0,0)
  HatchRotation = 0
  HatchScale = 1
  IsoCount = 0
  IsoHidden = false
  IsoVisible = true
  LockPosition = false
  NameGeomPattern = Diamant
  Perspective = false
  Rotation = 0
  Scale = 0.5
  ScaleType = 2
  ScrubCount = 0
  SeamHidden = false
  SeamVisible = true
  SectionDirection = 4
  SectionNormal = (1,0,0)
  SectionOrigin = (38,109,41.5)
  SmoothHidden = false
  SmoothVisible = true
  Source = -> [Body002]
  TrimAfterCut = false
  X = 146.365
  XDirection = (0,-1,0)
  Y = 48.7904
FEATURE [TechDraw::DrawViewSection] SectionView002  label="B-B"
  BaseView = -> ProjItem002
  CoarseView = false
  CutSurfaceDisplay = 2
  Direction = (1e-16,-1,0)
  FileGeomPattern = C:/Program Files/FreeCAD 0.21/data/Mod/TechDraw/PAT/FCPAT.pat
  FileHatchPattern = C:/Program Files/FreeCAD 0.21/data/Mod/TechDraw/Patterns/simple.svg
  Focus = 100
  FuseBeforeCut = false
  HardHidden = false
  HatchOffset = (0,0,0)
  HatchRotation = 0
  HatchScale = 1
  IsoCount = 0
  IsoHidden = false
  IsoVisible = true
  LockPosition = false
  NameGeomPattern = Diamant
  Perspective = false
  Rotation = 90
  Scale = 0.5
  ScaleType = 2
  ScrubCount = 0
  SeamHidden = false
  SeamVisible = true
  SectionDirection = 4
  SectionNormal = (1e-16,-1,0)
  SectionOrigin = (107,158,41.5)
  SmoothHidden = false
  SmoothVisible = true
  Source = -> [Body002]
  TrimAfterCut = false
  X = 46.1608
  XDirection = (1,1e-16,0)
  Y = 159.91
FEATURE [TechDraw::DrawViewAnnotation] Annotation
  Font = osifont
  LineSpace = 100
  LockPosition = false
  MaxWidth = -1
  Rotation = 0
  Scale = 0.5
  ScaleType = 0
  Text = A
  TextSize = 5
  TextStyle = 0
  X = 83.2039
  Y = 173.077
FEATURE [TechDraw::DrawViewAnnotation] Annotation001
  Font = osifont
  LineSpace = 100
  LockPosition = false
  MaxWidth = -1
  Rotation = 0
  Scale = 0.5
  ScaleType = 0
  Text = A
  TextSize = 5
  TextStyle = 0
  X = 208.088
  Y = 174.631
FEATURE [TechDraw::DrawViewDimension] Dimension029
  AngleOverride = false
  Arbitrary = true
  ArbitraryTolerances = false
  EqualTolerance = true
  ExtensionAngle = 0
  FormatSpec = 200
  FormatSpecOverTolerance = %+.2w
  FormatSpecUnderTolerance = %+.2w
  Inverted = false
  LineAngle = 0
  LockPosition = false
  MeasureType = 1
  OverTolerance = 0
  References2D = -> [ProjItem002]
  Rotation = 0
  Scale = 0.5
  ScaleType = 0
  TheoreticalExact = false
  Type = 0
  UnderTolerance = 0
  X = -31.4154
  Y = 29.5425
FEATURE [TechDraw::DrawViewDimension] Dimension030
  AngleOverride = false
  Arbitrary = false
  ArbitraryTolerances = false
  EqualTolerance = true
  ExtensionAngle = 0
  FormatSpec = %.2w
  FormatSpecOverTolerance = %+.2w
  FormatSpecUnderTolerance = %+.2w
  Inverted = false
  LineAngle = 0
  LockPosition = false
  MeasureType = 1
  OverTolerance = 0
  References2D = -> [ProjItem002]
  Rotation = 0
  Scale = 0.5
  ScaleType = 0
  TheoreticalExact = false
  Type = 0
  UnderTolerance = 0
  X = 46.1772
  Y = -21.4952
FEATURE [TechDraw::DrawViewDimension] Dimension031
  AngleOverride = false
  Arbitrary = false
  ArbitraryTolerances = false
  EqualTolerance = true
  ExtensionAngle = 0
  FormatSpec = %.2w
  FormatSpecOverTolerance = %+.2w
  FormatSpecUnderTolerance = %+.2w
  Inverted = false
  LineAngle = 0
  LockPosition = false
  MeasureType = 1
  OverTolerance = 0
  References2D = -> [ProjItem003]
  Rotation = 0
  Scale = 0.5
  ScaleType = 0
  TheoreticalExact = false
  Type = 1
  UnderTolerance = 0
  X = -0.796508
  Y = -67.4652
FEATURE [TechDraw::DrawViewDimension] Dimension032
  AngleOverride = false
  Arbitrary = false
  ArbitraryTolerances = false
  EqualTolerance = true
  ExtensionAngle = 0
  FormatSpec = %.2w
  FormatSpecOverTolerance = %+.2w
  FormatSpecUnderTolerance = %+.2w
  Inverted = false
  LineAngle = 0
  LockPosition = false
  MeasureType = 1
  OverTolerance = 0
  References2D = -> [ProjItem003]
  Rotation = 0
  Scale = 0.5
  ScaleType = 0
  TheoreticalExact = false
  Type = 1
  UnderTolerance = 0
  X = -1.40698
  Y = -81.07
FEATURE [TechDraw::DrawViewDimension] Dimension033
  AngleOverride = false
  Arbitrary = false
  ArbitraryTolerances = false
  EqualTolerance = true
  ExtensionAngle = 0
  FormatSpec = %.2w
  FormatSpecOverTolerance = %+.2w
  FormatSpecUnderTolerance = %+.2w
  Inverted = false
  LineAngle = 0
  LockPosition = false
  MeasureType = 1
  OverTolerance = 0
  References2D = -> [ProjItem003]
  Rotation = 0
  Scale = 0.5
  ScaleType = 0
  TheoreticalExact = false
  Type = 1
  UnderTolerance = 0
  X = -5.05223
  Y = 66.0233
FEATURE [TechDraw::DrawViewDimension] Dimension034
  AngleOverride = false
  Arbitrary = false
  ArbitraryTolerances = false
  EqualTolerance = true
  ExtensionAngle = 0
  FormatSpec = %.2w
  FormatSpecOverTolerance = %+.2w
  FormatSpecUnderTolerance = %+.2w
  Inverted = false
  LineAngle = 0
  LockPosition = false
  MeasureType = 1
  OverTolerance = 0
  References2D = -> [ProjItem003]
  Rotation = 0
  Scale = 0.5
  ScaleType = 0
  TheoreticalExact = false
  Type = 1
  UnderTolerance = 0
  X = 31.8722
  Y = 65.5698
FEATURE [TechDraw::DrawViewAnnotation] Annotation002
  Font = osifont
  LineSpace = 100
  LockPosition = false
  MaxWidth = -1
  Rotation = 0
  Scale = 0.5
  ScaleType = 0
  Text = B
  TextSize = 5
  TextStyle = 0
  X = 136.903
  Y = 254.449
FEATURE [TechDraw::DrawViewAnnotation] Annotation003
  Font = osifont
  LineSpace = 100
  LockPosition = false
  MaxWidth = -1
  Rotation = 0
  Scale = 0.5
  ScaleType = 0
  Text = B
  TextSize = 5
  TextStyle = 0
  X = 135.809
  Y = 129.906
FEATURE [TechDraw::DrawViewAnnotation] Annotation004
  Font = osifont
  LineSpace = 100
  LockPosition = false
  MaxWidth = -1
  Rotation = 0
  Scale = 0.5
  ScaleType = 0
  Text = VUE DE GAUCHE
  TextSize = 5
  TextStyle = 0
  X = 303.694
  Y = 276.661
FEATURE [TechDraw::DrawViewAnnotation] Annotation005
  Font = osifont
  LineSpace = 100
  LockPosition = false
  MaxWidth = -1
  Rotation = 0
  Scale = 0.5
  ScaleType = 0
  Text = VUE DE FACE
  TextSize = 5
  TextStyle = 0
  X = 150.774
  Y = 277.147
FEATURE [TechDraw::DrawViewAnnotation] Annotation006
  Font = osifont
  LineSpace = 100
  LockPosition = false
  MaxWidth = -1
  Rotation = 0
  Scale = 0.5
  ScaleType = 0
  Text = B - B
  TextSize = 5
  TextStyle = 0
  X = 44.1231
  Y = 203.143
FEATURE [TechDraw::DrawViewAnnotation] Annotation007
  Font = osifont
  LineSpace = 100
  LockPosition = false
  MaxWidth = -1
  Rotation = 0
  Scale = 0.5
  ScaleType = 0
  Text = A - A
  TextSize = 5
  TextStyle = 0
  X = 142.457
  Y = 83.3906
FEATURE [TechDraw::DrawSVGTemplate] Template002
  Height = 297
  Orientation = 1
  Template = C:/Program Files/FreeCAD 0.21/data/Mod/TechDraw/Templates/A3_Landscape_FR_m52.svg
  Width = 420
FEATURE [TechDraw::DrawProjGroupItem] ProjItem004  label="Front002"
  CoarseView = false
  Direction = (0,0,1)
  Focus = 100
  HardHidden = false
  IsoCount = 0
  IsoHidden = false
  IsoVisible = true
  LockPosition = true
  Perspective = false
  Rotation = 0
  RotationVector = (1,0,0)
  ScaleType = 2
  ScrubCount = 0
  SeamHidden = false
  SeamVisible = true
  SmoothHidden = false
  SmoothVisible = true
  Source = -> [Body003]
  Type = 0
  X = 0
  XDirection = (1e-16,-1,0)
  Y = 0
FEATURE [TechDraw::DrawProjGroup] ProjGroup002
  Anchor = -> ProjItem004
  AutoDistribute = true
  LockPosition = false
  ProjectionType = 0
  Rotation = 0
  Scale = 0.5
  ScaleType = 0
  Source = -> [Body003]
  Views = -> [ProjItem004]
  X = 130.8
  Y = 175.257
  spacingX = 15
  spacingY = 15
FEATURE [TechDraw::DrawViewDimension] Dimension035
  AngleOverride = false
  Arbitrary = false
  ArbitraryTolerances = false
  EqualTolerance = true
  ExtensionAngle = 0
  FormatSpec = %.2w
  FormatSpecOverTolerance = %+.2w
  FormatSpecUnderTolerance = %+.2w
  Inverted = false
  LineAngle = 0
  LockPosition = false
  MeasureType = 1
  OverTolerance = 0
  References2D = -> [ProjItem004]
  Rotation = 0
  Scale = 0.5
  ScaleType = 0
  TheoreticalExact = false
  Type = 2
  UnderTolerance = 0
  X = 71.9206
  Y = -38.7904
FEATURE [TechDraw::DrawViewDimension] Dimension036
  AngleOverride = false
  Arbitrary = false
  ArbitraryTolerances = false
  EqualTolerance = true
  ExtensionAngle = 0
  FormatSpec = %.2w
  FormatSpecOverTolerance = %+.2w
  FormatSpecUnderTolerance = %+.2w
  Inverted = false
  LineAngle = 0
  LockPosition = false
  MeasureType = 1
  OverTolerance = 0
  References2D = -> [ProjItem004]
  Rotation = 0
  Scale = 0.5
  ScaleType = 0
  TheoreticalExact = false
  Type = 1
  UnderTolerance = 0
  X = 28.2581
  Y = -68.6308
FEATURE [TechDraw::DrawViewAnnotation] Annotation008
  Font = osifont
  LineSpace = 100
  LockPosition = false
  MaxWidth = -1
  Rotation = 0
  Scale = 0.5
  ScaleType = 0
  Text = Pour le triangle gauche, il faut reprendre  | les dimensions du triangle droit. | Seul le placement de l'entretoise et | des trous taraudés ont changés.
  TextSize = 5
  TextStyle = 0
  X = 288.712
  Y = 193.017
FEATURE [TechDraw::DrawPage] Page002
  KeepUpdated = true
  NextBalloonIndex = 1
  ProjectionType = 0
  Scale = 0.5
  Template = -> Template002
  Views = -> [ProjGroup002,Dimension035,Dimension036,Annotation008]
FEATURE [TechDraw::DrawViewAnnotation] Annotation009
  Font = osifont
  LineSpace = 100
  LockPosition = false
  MaxWidth = -1
  Rotation = 0
  Scale = 0.5
  ScaleType = 0
  Text = Mat : ACIER | Peinture : JAUNE
  TextSize = 5
  TextStyle = 0
  X = 373.284
  Y = 201.952
FEATURE [TechDraw::DrawViewAnnotation] Annotation010
  Font = osifont
  LineSpace = 100
  LockPosition = false
  MaxWidth = -1
  Rotation = 0
  Scale = 0.5
  ScaleType = 0
  Text = L'entretoise est soudée | aux faces
  TextSize = 5
  TextStyle = 0
  X = 374.016
  Y = 142.642
FEATURE [TechDraw::DrawViewBalloon] Balloon
  BubbleShape = 6
  EndType = 0
  EndTypeScale = 1
  KinkLength = 5
  LockPosition = false
  OriginX = -41.32
  OriginY = 0.0492348
  Rotation = 0
  Scale = 0.5
  ScaleType = 0
  ShapeScale = 1
  SourceView = -> ProjItem003
  Text = Pas de dépacement
  TextWrapLen = -1
  X = -112.363
  Y = 94.252
FEATURE [TechDraw::DrawPage] Page001
  KeepUpdated = true
  NextBalloonIndex = 2
  ProjectionType = 0
  Scale = 0.5
  Template = -> Template001
  Views = -> [ProjGroup001,Dimension019,Dimension020,Dimension021,Dimension022,Dimension023,Dimension024,Dimension025,Dimension026,Dimension027,Dimension028,SectionView001,SectionView002,Annotation,Annotation001,Dimension029,Dimension030,Dimension031,Dimension032,Dimension033,Dimension034,Annotation002,Annotation003,Annotation004,Annotation005,Annotation006,Annotation007,Annotation009,Annotation010,Balloon]
